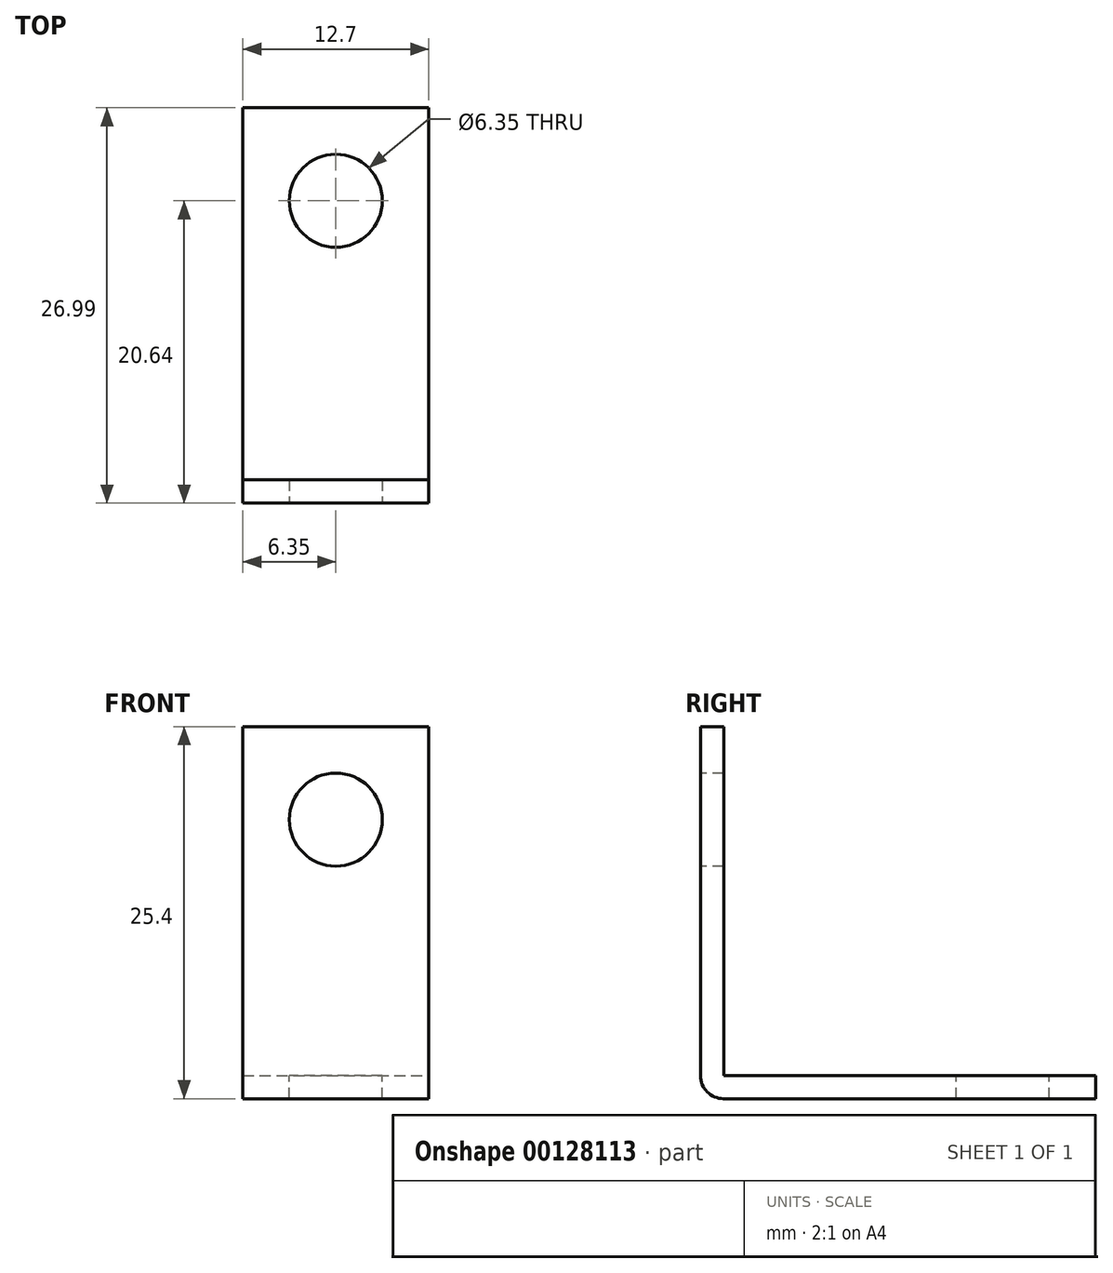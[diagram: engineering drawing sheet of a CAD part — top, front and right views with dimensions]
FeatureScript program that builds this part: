
annotation { "Feature Type Name" : "Feature", "Feature Type Description" : "" }
export const myFeature = defineFeature(function(context is Context, id is Id, definition is map)
    precondition{}
    {
        {
            var Q0;
            Q0=qCreatedBy(makeId("Front.planeOp"),FACE);
            cPlane(context, id + "F0", {"entities" : qUnion([Q0]), "cplaneType" : CPlaneType.OFFSET, "offset" : 1.59 * mm, "width" : 152.4 * mm, "height" : 152.4 * mm});
        }
        {
            var Q0;
            Q0=qCreatedBy(id+"F0.planeOp",FACE);
            var sketch = newSketch(context, id + "F1", { "sketchPlane" : qUnion([Q0])});
            skLineSegment(sketch, "E0", {"start": v(0, 0) * mm, "end": v(-6.35, 0) * mm});
            skLineSegment(sketch, "E1", {"start": v(-6.35, 0) * mm, "end": v(-6.35, -25.4) * mm});
            skLineSegment(sketch, "E2", {"start": v(-6.35, -25.4) * mm, "end": v(6.35, -25.4) * mm});
            skLineSegment(sketch, "E3", {"start": v(6.35, -25.4) * mm, "end": v(6.35, 0) * mm});
            skLineSegment(sketch, "E4", {"start": v(6.35, 0) * mm, "end": v(0, 0) * mm});
            skLineSegment(sketch, "E5", {"start": v(-6.35, -25.4) * mm, "end": v(-6.35, -23.81) * mm});
            skLineSegment(sketch, "E6", {"start": v(-6.35, -23.81) * mm, "end": v(6.35, -23.81) * mm});
            skLineSegment(sketch, "E7", {"start": v(6.35, -23.81) * mm, "end": v(6.35, -25.4) * mm});
            skCircle(sketch, "E8", {"center": v(0, -6.35) * mm, "radius": 3.18 * mm});
            skSolve(sketch);
        }
        {
            var Q0;
            Q0=makeQuery(id+"F1.imprint","IMPRINT",FACE,{"disambiguationData":[TD([[makeQuery(id+"F1.imprint","IMPRINT",EDGE,{"derivedFrom":sQuery(id+"F1.wireOp",EDGE,"E0")}),1.0]])]});
            extrude(context, id + "F2", {"entities" : qUnion([Q0]), "oppositeDirection" : true, "depth" : 1.59 * mm});
        }
        {
            var Q0;
            Q0=makeQuery(id+"F1.imprint","IMPRINT",FACE,{"disambiguationData":[TD([[makeQuery(id+"F1.imprint","IMPRINT",EDGE,{"derivedFrom":sQuery(id+"F1.wireOp",EDGE,"E2")}),1.0]])]});
            extrude(context, id + "F3", {"entities" : qUnion([Q0]), "operationType" : NewBodyOperationType.ADD, "oppositeDirection" : true, "depth" : 26.99 * mm});
        }
        {
            var Q0;
            Q0=makeQuery(id+"F3.opExtrude","SWEPT_FACE",FACE,{"disambiguationData":[OSD([sQuery(id+"F1.wireOp",EDGE,"E6")])]});
            var sketch = newSketch(context, id + "F4", { "sketchPlane" : qUnion([Q0])});
            skPoint(sketch, "E9.endSnap0", {"position": v(0, 25.4) * mm});
            skCircle(sketch, "E10", {"center": v(0, 19.05) * mm, "radius": 3.18 * mm});
            skSolve(sketch);
        }
        {
            var Q0;
            Q0 = qSketchRegion(id + "F4", true);
            extrude(context, id + "F5", {"entities" : qUnion([Q0]), "operationType" : NewBodyOperationType.REMOVE, "oppositeDirection" : true, "depth" : 1.59 * mm});
        }
        {
            var Q0;
            Q0=makeQuery(id+"F3.opExtrude","CAP_EDGE",EDGE,{"disambiguationData":[OSD([sQuery(id+"F1.wireOp",EDGE,"E2")])],"isStart":true});
            fillet(context, id + "F6", {"entities" : qUnion([Q0]), "radius" : 1.58 * mm, "tangentPropagation" : true, "allowEdgeOverflow" : false});
        }
    });
